# Revit family: ASL_Plus_Series_Head & Floor_Track_64mm_Stud
name_source: partatom
category: Detail Items
revit_build: Autodesk Revit 2018 (Build: 20170223_1515(x64)
units: mm (PartAtom-declared; Revit-internal decimal feet)

## family parameters
Rotate with component = No
Section Shape = Not Defined
Shared = Yes

## types (4) — shared parameters
Manufacturer = Aluminate Solutions Limited
Technical Info = www.aluminate.nz
Type Comments = Plus Series

## per-type parameters (varying)
| type | Headsection&Floor Track_ASL_754 | Headsection&Floor Track_ASL_757 | Headsection&Floor Track_ASL_758 | Headsection_ASL_740 | Plastboard Movement | PlasterBoard_3 | Plasterboard Depth | Plasterboard Movement | Steel Stud Movement |
| 25mm Negative Head & Floor Track 64mm Stud 2x13mm Gib Ext 13mm Gib Int | No | No | Yes | No | 39 mm | Yes | 62 mm | 29 mm  [stored 0.0951444 ft] | 39 mm |
| Negative Head 64mm Stud 13mm Gib BS | No | No | No | Yes | 31 mm | No | 49 mm | 34 mm | 32 mm |
| 25mm Negative Head & Floor 64mm Stud 12mm Gib BS | Yes | No | No | No | 31 mm | No | 62 mm | 34 mm | 32 mm |
| 13mm Negative Head & Floor Track 64mm Stud 2x13mm Gib Ext 13mm Gib Int | No | Yes | No | No | 39 mm | Yes | 50 mm | 29 mm  [stored 0.0951444 ft] | 39 mm |

note: [stored X ft] marks values corroborated as IEEE doubles in the binary element streams (Revit-internal decimal feet)

## geometry (parser evidence)
native form markers: Sweep x3
no freeform markers — native parametric forms only
